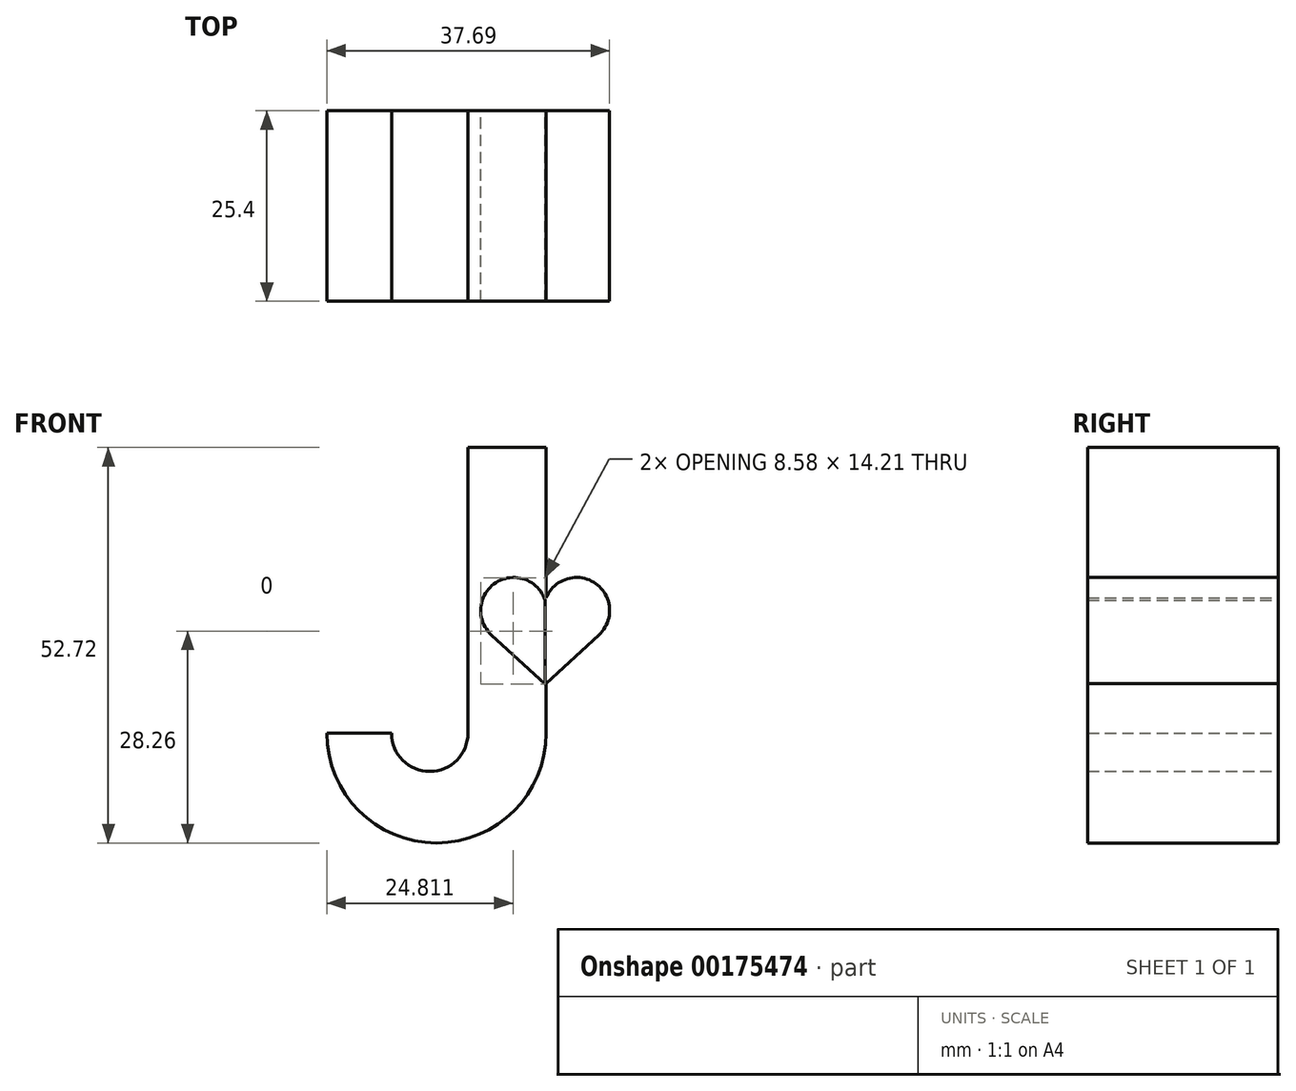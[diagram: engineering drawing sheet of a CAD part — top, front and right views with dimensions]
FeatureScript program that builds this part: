
annotation { "Feature Type Name" : "Feature", "Feature Type Description" : "" }
export const myFeature = defineFeature(function(context is Context, id is Id, definition is map)
    precondition{}
    {
        {
            var Q0;
            Q0=qCreatedBy(makeId("Front.planeOp"),FACE);
            var sketch = newSketch(context, id + "F0", { "sketchPlane" : qUnion([Q0])});
            skLineSegment(sketch, "E0", {"start": v(0, 0) * mm, "end": v(0, 38.1) * mm});
            skArc(sketch, "E1", {"start": v(-29.23, 0) * mm, "mid": v(-14.62, -14.62) * mm, "end": v(0, 0) * mm});
            skLineSegment(sketch, "E2", {"start": v(0, 38.1) * mm, "end": v(-10.42, 38.1) * mm});
            skLineSegment(sketch, "E3", {"start": v(-10.42, 38.1) * mm, "end": v(-10.42, 0) * mm});
            skArc(sketch, "E4", {"start": v(-20.6, 0) * mm, "mid": v(-15.51, -5.09) * mm, "end": v(-10.42, 0) * mm});
            skLineSegment(sketch, "E5", {"start": v(-20.6, 0) * mm, "end": v(-29.23, 0) * mm});
            skLineSegment(sketch, "E6", {"start": v(-0.13, 6.53) * mm, "end": v(-7.3, 13.13) * mm});
            skLineSegment(sketch, "E7", {"start": v(-0.13, 6.53) * mm, "end": v(-0.13, 17.72) * mm});
            skArc(sketch, "E8", {"start": v(-0.13, 17.72) * mm, "mid": v(-6.7, 20.08) * mm, "end": v(-7.3, 13.13) * mm});
            skLineSegment(sketch, "E9", {"start": v(-0.13, 17.72) * mm, "end": v(-0.13, 17.72) * mm});
            skPoint(sketch, "E10", {"position": v(-0.13, 12.12) * mm});
            skLineSegment(sketch, "E11.MirrorCS", {"start": v(-0.13, 6.53) * mm, "end": v(7.04, 13.13) * mm});
            skArc(sketch, "E12.MirrorCS", {"start": v(-0.13, 17.72) * mm, "mid": v(6.43, 20.08) * mm, "end": v(7.04, 13.13) * mm});
            skSolve(sketch);
        }
        {
            var Q0;
            {var subQ1=sQuery(id+"F0.wireOp",EDGE,"E1");Q0=makeQuery(id+"F0.imprint","IMPRINT",FACE,{"disambiguationData":[TD([[makeQuery(id+"F0.imprint","IMPRINT",EDGE,{"derivedFrom":subQ1}),1.0]])]});}
            var Q1;
            Q1=makeQuery(id+"F0.imprint","IMPRINT",FACE,{"disambiguationData":[TD([[makeQuery(id+"F0.imprint","IMPRINT",EDGE,{"derivedFrom":sQuery(id+"F0.wireOp",EDGE,"E7")}),-1.0]])]});
            var Q2;
            {var subQ0=sQuery(id+"F0.wireOp",EDGE,"E11.MirrorCS");var subQ1=sQuery(id+"F0.wireOp",EDGE,"E0");var subQ2=makeQuery(id+"F0.imprint","INTERSECT",VERTEX,{"derivedFrom":[subQ1,subQ0]});Q2=makeQuery(id+"F0.imprint","IMPRINT",FACE,{"disambiguationData":[TD([[makeQuery(id+"F0.imprint","IMPRINT",EDGE,{"disambiguationData":[TD([[subQ2,-1.0]])],"derivedFrom":subQ1}),-1.0]])]});}
            extrude(context, id + "F1", {"entities" : qUnion([Q0, Q1, Q2]), "depth" : 25.4 * mm});
        }
    });
